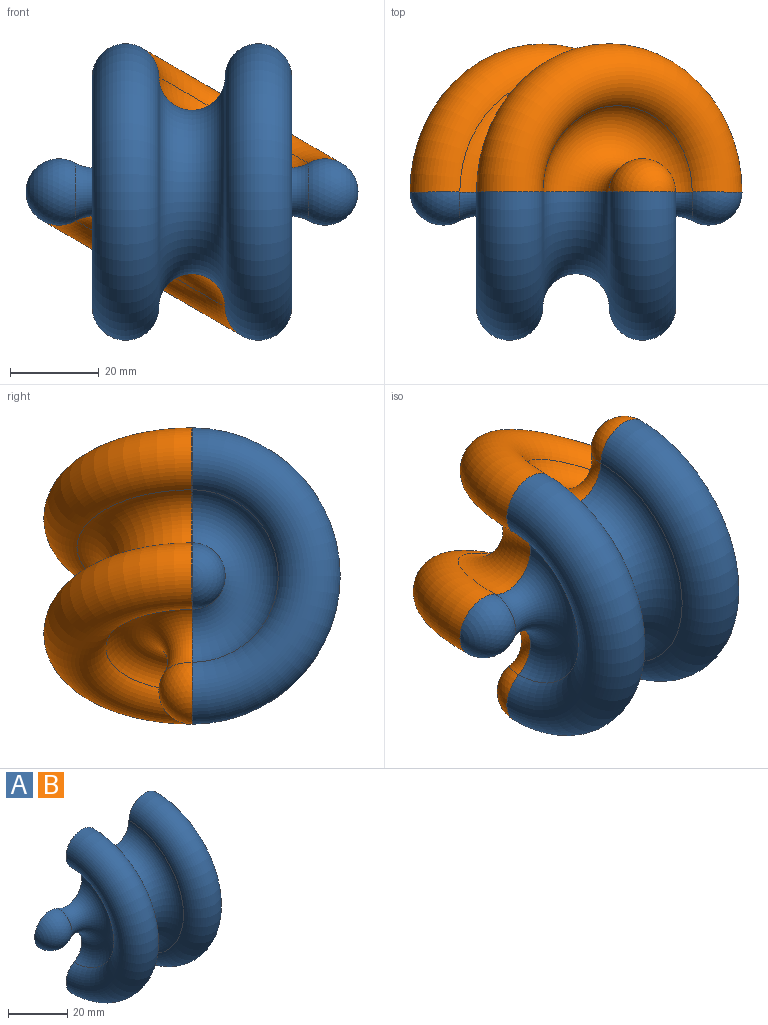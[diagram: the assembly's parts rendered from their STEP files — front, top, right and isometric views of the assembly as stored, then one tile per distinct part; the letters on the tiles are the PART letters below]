
ASSEMBLY  parts=2 mates=1
PART A: 8 faces, bbox 75x36.2x72.5 mm
  f0: torus R=25.98mm, axis (-1,0,0), area 1569.7mm2, adj f1,f6,f7
  f1: torus R=25.98mm, axis (-1,0,0), area 2829.3mm2, adj f0,f2,f7
  f2: torus R=12.99mm, axis (-1,0,0), area 784.9mm2, adj f1,f3,f7
  f3: sphere r=7.5mm, area 265.1mm2, adj f2,f7
  f4: sphere r=7.5mm, area 265.1mm2, adj f5,f7
  f5: torus R=12.99mm, axis (-1,0,0), area 784.9mm2, adj f4,f6,f7
  f6: torus R=25.98mm, axis (-1,0,0), area 2829.3mm2, adj f0,f5,f7
  f7: plane 75x66.96mm, normal (0,1,0), area 2515mm2, adj f0,f1,f2,f3,f4,f5,f6
PART B: same geometry as A
PLACE A at identity fixed
PLACE B rot(axis=(0.5,0,-0.87),180deg) t=(0,0,0)mm
MATE parallel B.f7 <-> A.f7  axis (0,-1,0) through (0,0,0)mm
